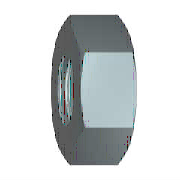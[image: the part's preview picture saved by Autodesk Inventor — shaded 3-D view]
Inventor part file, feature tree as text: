
AUTODESK INVENTOR PART (.ipt)
format: ipt  version: 2025 (Build 290162010, 162A)  size: 167,424 bytes
history: native  units: mm (DEFAULTED — no unit token found)
features: chamfer x1, hole x1, other x1, plane x1
ambient origin geometry x7: Origin, YZ Plane, XZ Plane, X Axis, Y Axis, Z Axis, Center Point
bodies: Solid1 (feature_tree), Body (feature_tree)
feature tree (4):
  chamfer  "Chamfer1"  Distance=20.78461mm
  hole  "Thread"  [1 undecoded]
  other  "Work Axis1"
  plane  "Work Plane1"
note: 1 required parameter value undecoded (feature->parameter linkage not recoverable at this tier; creation-order binding heuristic only, values carry confidence <= 0.55)
